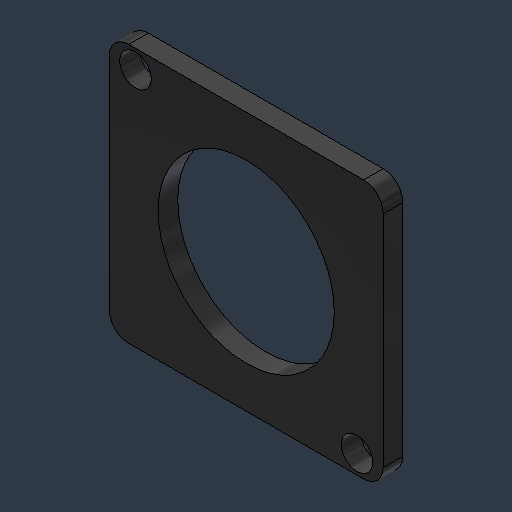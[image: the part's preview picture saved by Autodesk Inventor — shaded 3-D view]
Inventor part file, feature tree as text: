
AUTODESK INVENTOR PART (.ipt)
format: ipt  version: 2024.3 (Build 283343000, 343)  size: 126,976 bytes
history: native  units: mm (DEFAULTED — no unit token found)
features: sketch x3, hole x2, extrude x1, fillet x1
ambient origin geometry x8: Origin, YZ Plane, XZ Plane, XY Plane, X Axis, Y Axis, Z Axis, Center Point
bodies: Solid1 (feature_tree)
feature tree (7):
  extrude  "Extrusion1"  Depth=42.0116mm
  hole  "Hole1"  [1 undecoded]
  hole  "Hole2"  [1 undecoded]
  fillet  "Fillet1"  Radius=3.175mm
  sketch  "Sketch2"  dims[d0=44.45mm d1=42.0116mm]
  sketch  "Sketch3"  dims[d2=3.175mm d3=0.0mm]
  sketch  "Sketch4"  dims[d4=28.575mm d5=9.652mm d6=9.525mm d7=6.35mm d8=14.3117mm d9=25.4mm d10=20.594885mm d11=45.0deg d12=50.8mm d13=5.1054mm d14=19.05mm d15=9.779mm d16=1.9558mm d17=14.3117mm d18=25.4mm d19=20.594885mm d20=3.175mm]
note: 2 required parameter values undecoded (feature->parameter linkage not recoverable at this tier; creation-order binding heuristic only, values carry confidence <= 0.55)
